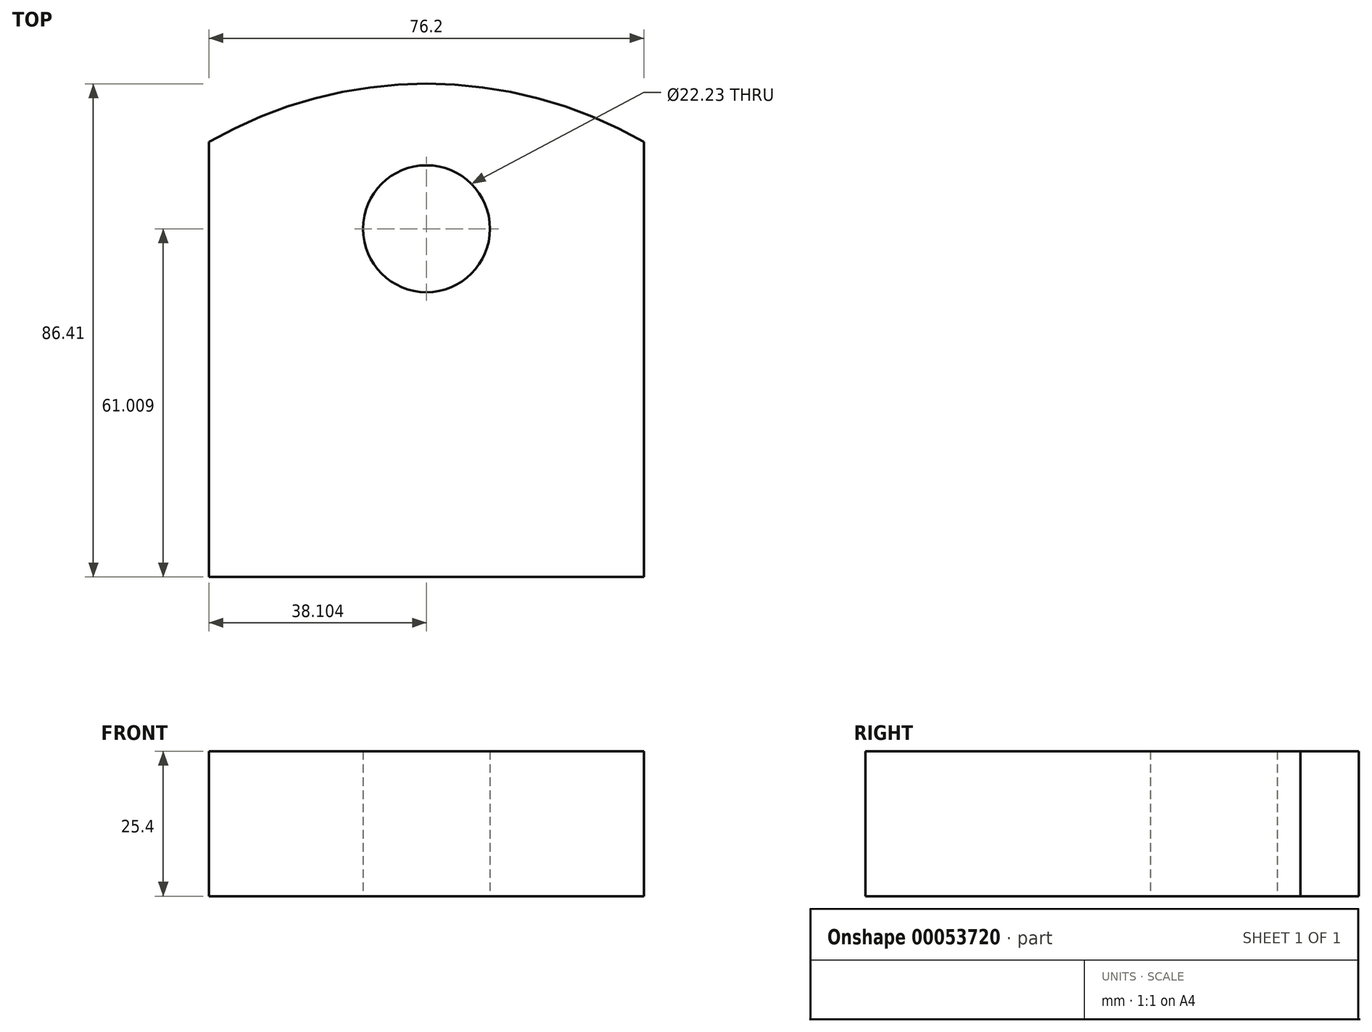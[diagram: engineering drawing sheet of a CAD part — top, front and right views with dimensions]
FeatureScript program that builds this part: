
annotation { "Feature Type Name" : "Feature", "Feature Type Description" : "" }
export const myFeature = defineFeature(function(context is Context, id is Id, definition is map)
    precondition{}
    {
        {
            var Q0;
            Q0=qCreatedBy(makeId("Top.planeOp"),FACE);
            var sketch = newSketch(context, id + "F0", { "sketchPlane" : qUnion([Q0])});
            skLineSegment(sketch, "E0", {"start": v(-73.59, 0) * mm, "end": v(2.61, 0) * mm});
            skLineSegment(sketch, "E1", {"start": v(2.61, 0) * mm, "end": v(2.61, 76.2) * mm});
            skLineSegment(sketch, "E2", {"start": v(-73.59, 0) * mm, "end": v(-73.59, 76.2) * mm});
            skArc(sketch, "E3", {"start": v(2.61, 76.2) * mm, "mid": v(-35.49, 86.4) * mm, "end": v(-73.59, 76.2) * mm});
            skCircle(sketch, "E4", {"center": v(-35.49, 61) * mm, "radius": 11.11 * mm});
            skPoint(sketch, "E4.centerSnap0", {"position": v(-35.49, 86.4) * mm});
            skSolve(sketch);
        }
        {
            var Q0;
            Q0=makeQuery(id+"F0.imprint","IMPRINT",FACE,{"disambiguationData":[TD([[makeQuery(id+"F0.imprint","IMPRINT",EDGE,{"derivedFrom":sQuery(id+"F0.wireOp",EDGE,"E0")}),1.0]])]});
            extrude(context, id + "F1", {"entities" : qUnion([Q0]), "depth" : 25.4 * mm});
        }
    });
